FCSTD DOCUMENT  (FreeCAD 0.21R32532 (Git))
Label: composit_stand4-small-main-sketches
License: All rights reserved
LicenseURL: http://en.wikipedia.org/wiki/All_rights_reserved
objects: Sketcher::SketchObject×1, Spreadsheet::Sheet×1
note: 1 computed .brp shape members not serialized (recipe doc carries the construction recipe); baked Part::Feature solids carry a one-line shape summary decoded from their .brp
EXTERNAL_REF file=composit-properties.FCStd obj=Spreadsheet
EXTERNAL_REF file=composit_stand-main-sketches.FCStd obj=Spreadsheet
EXTERNAL_REF file=basin_small.FCStd obj=Spreadsheet
EXTERNAL_REF file=module.FCStd obj=Spreadsheet

FEATURE [Sketcher::SketchObject] Sketch
  FullyConstrained = true
  MapMode = 5
  expr: Constraints[38] = <<composit_stand-main-sketches>>#<<Properties>>.end_face_width
  expr: Constraints[39] = <<composit-properties>>#<<Properties>>.thickness
  expr: Constraints[40] = <<Properties>>.plane_width
  expr: Constraints[43] = <<composit-properties>>#<<Properties>>.al_thickness
  sketch-geometry (18):
    g0: LineSegment StartX=14.5 StartY=8.66025 StartZ=0 EndX=14.5 EndY=206.372 EndZ=0
    g1: LineSegment StartX=14.5 StartY=206.372 StartZ=0 EndX=-14.5 EndY=206.372 EndZ=0
    g2: LineSegment StartX=-14.5 StartY=206.372 StartZ=0 EndX=-14.5 EndY=8.37158 EndZ=0
    g3: LineSegment StartX=-14.5 StartY=8.37158 StartZ=0 EndX=-185.973 EndY=-90.6284 EndZ=0
    g4: LineSegment StartX=-185.973 StartY=-90.6284 StartZ=0 EndX=-171.473 EndY=-115.743 EndZ=0
    g5: LineSegment StartX=-171.473 StartY=-115.743 StartZ=0 EndX=1.87299e-11 EndY=-16.7432 EndZ=0
    g6: LineSegment StartX=1.87299e-11 StartY=-16.7432 StartZ=0 EndX=171.473 EndY=-115.743 EndZ=0
    g7: LineSegment StartX=171.473 StartY=-115.743 StartZ=0 EndX=185.973 EndY=-90.6285 EndZ=0
    g8: LineSegment StartX=185.973 StartY=-90.6285 StartZ=0 EndX=11.5 EndY=10.1036 EndZ=0
    g9: LineSegment StartX=11.5 StartY=10.1036 StartZ=0 EndX=11.5 EndY=25.1036 EndZ=0
    g10: LineSegment StartX=1.87299e-11 StartY=-16.7432 StartZ=0 EndX=-1.25881e-11 EndY=3.0365e-11 EndZ=0
    g11: LineSegment StartX=-1.25881e-11 StartY=3.0365e-11 StartZ=0 EndX=14.5 EndY=8.37158 EndZ=0
    g12: LineSegment StartX=14.5 StartY=8.37158 StartZ=0 EndX=-14.5 EndY=8.37158 EndZ=0
    g13: LineSegment StartX=-14.5 StartY=8.37158 StartZ=0 EndX=1.87317e-11 EndY=-16.7432 EndZ=0
    g14: LineSegment StartX=1.87299e-11 StartY=-16.7432 StartZ=0 EndX=14.5 EndY=8.37158 EndZ=0
    g15: LineSegment StartX=-1.25881e-11 StartY=3.0365e-11 StartZ=0 EndX=-14.5 EndY=8.37158 EndZ=0
    g16: LineSegment StartX=14.5 StartY=8.66025 StartZ=0 EndX=14.2 EndY=8.66025 EndZ=0
    g17: LineSegment StartX=14.15 StartY=8.57365 StartZ=0 EndX=14.2 EndY=8.66025 EndZ=0
  constraints (52):
    c: Vertical(g0)
    c: Coincident(g0,g1)
    c: Horizontal(g1)
    c: Coincident(g1,g2)
    c: Vertical(g2)
    c: Coincident(g2,g3)
    c: Coincident(g3,g4)
    c: Coincident(g4,g5)
    c: PointOnObject(g5,g-2)
    c: Coincident(g5,g6)
    c: Coincident(g6,g7)
    c: Coincident(g7,g8)
    c: Coincident(g8,g9)
    c: Vertical(g9)
    c: Perpendicular(g7,g8)
    c: Perpendicular(g6,g7)
    c: Perpendicular(g4,g5)
    c: Perpendicular(g3,g4)
    c: Equal(g7,g4)
    c: Equal(g4,g1)
    c: Equal(g6,g5)
    c: Equal(g3,g2)
    c: Coincident(g5,g10)
    c: Coincident(g10,g-1)
    c: Coincident(g10,g11)
    c: PointOnObject(g11,g8)
    c: Coincident(g11,g12)
    c: Coincident(g12,g2)
    c: Coincident(g12,g13)
    c: Coincident(g13,g10)
    c: Coincident(g5,g14)
    c: Coincident(g14,g11)
    c: Coincident(g10,g15)
    c: Coincident(g15,g2)
    c: PointOnObject(g11,g0)
    c: Equal(g15,g10)
    c: Equal(g10,g11)
    c: Equal(g13,g12)
    c: DistanceX(g1,g1) = 29
    c: DistanceX(g8,g0) = 3
    c: DistanceY(g2,g2) = 198
    c: Coincident(g16,g0)
    c: Horizontal(g16)
    c: DistanceX(g16,g16) = 0.3
    c: DistanceY(g9,g9) = 15
    c: PointOnObject(g17,g8)
    c: Coincident(g17,g16)
    c: Perpendicular(g8,g17)
    c: Distance(g17) = 0.1
    c: Equal(g14,g12)
    c: DistanceY(g11) = 8.37158  'petall_dist'
    c: DistanceY(g10,g10) = 16.7432  'petal_side_connection'
FEATURE [Spreadsheet::Sheet] Spreadsheet  label="Properties"
  cells = B2(NumberOfModules)=6; C2(plane_width)==modules_distance_from_center + <<module>>#<<Properties>>.module_width / 2 + 25 mm; D2(total_height)==600 mm; E2(basin_height)==<<basin_small>>#<<Properties>>.rowHeights; F2(modules_distance_from_center)==<<module>>#<<Properties>>.module_width / 2 + 25 mm
